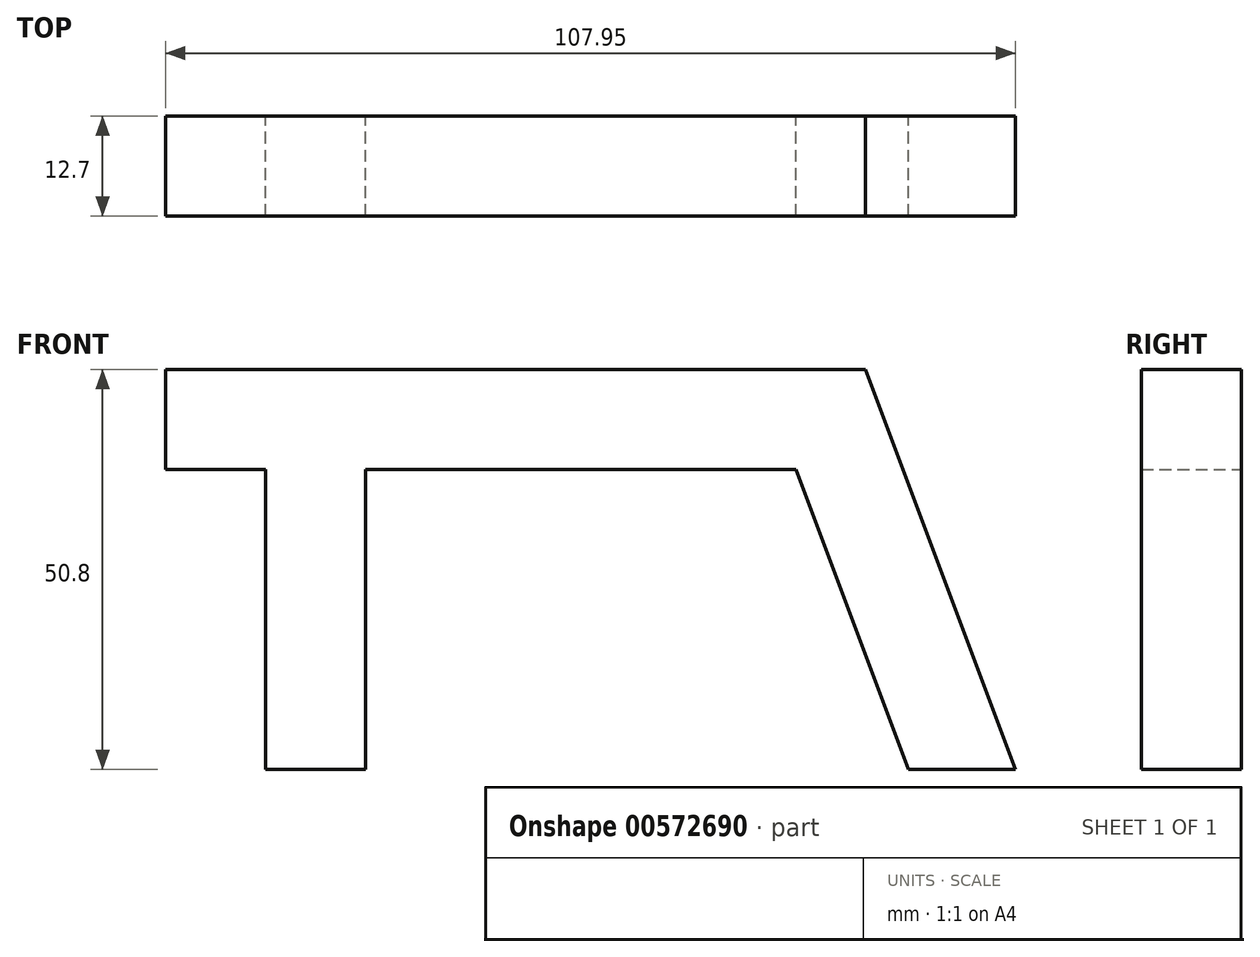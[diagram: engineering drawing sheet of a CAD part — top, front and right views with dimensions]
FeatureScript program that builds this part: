
annotation { "Feature Type Name" : "Feature", "Feature Type Description" : "" }
export const myFeature = defineFeature(function(context is Context, id is Id, definition is map)
    precondition{}
    {
        {
            var Q0;
            Q0=qCreatedBy(makeId("Front.planeOp"),FACE);
            var sketch = newSketch(context, id + "F0", { "sketchPlane" : qUnion([Q0])});
            skLineSegment(sketch, "E0", {"start": v(-47.2, 0) * mm, "end": v(48.06, 0) * mm});
            skLineSegment(sketch, "E1", {"start": v(-47.2, 0) * mm, "end": v(-47.2, 38.1) * mm});
            skLineSegment(sketch, "E2", {"start": v(-47.2, 38.1) * mm, "end": v(-59.9, 38.1) * mm});
            skLineSegment(sketch, "E3", {"start": v(-59.9, 38.1) * mm, "end": v(-59.9, 50.8) * mm});
            skLineSegment(sketch, "E4", {"start": v(-59.9, 50.8) * mm, "end": v(29, 50.8) * mm});
            skLineSegment(sketch, "E5", {"start": v(29, 50.8) * mm, "end": v(48.06, 0) * mm});
            skLineSegment(sketch, "E6", {"start": v(-34.5, 0) * mm, "end": v(-34.5, 38.1) * mm});
            skLineSegment(sketch, "E7", {"start": v(-34.5, 38.1) * mm, "end": v(20.2, 38.1) * mm});
            skLineSegment(sketch, "E8", {"start": v(20.2, 38.1) * mm, "end": v(34.5, 0) * mm});
            skSolve(sketch);
        }
        {
            var Q0;
            {var subQ0=sQuery(id+"F0.wireOp",EDGE,"E1");Q0=makeQuery(id+"F0.imprint","IMPRINT",FACE,{"disambiguationData":[TD([[makeQuery(id+"F0.imprint","IMPRINT",EDGE,{"derivedFrom":subQ0}),-1.0]])]});}
            extrude(context, id + "F1", {"entities" : qUnion([Q0]), "endBound" : BoundingType.SYMMETRIC, "depth" : 12.7 * mm, "offsetDistance" : 25.4 * mm});
        }
    });
